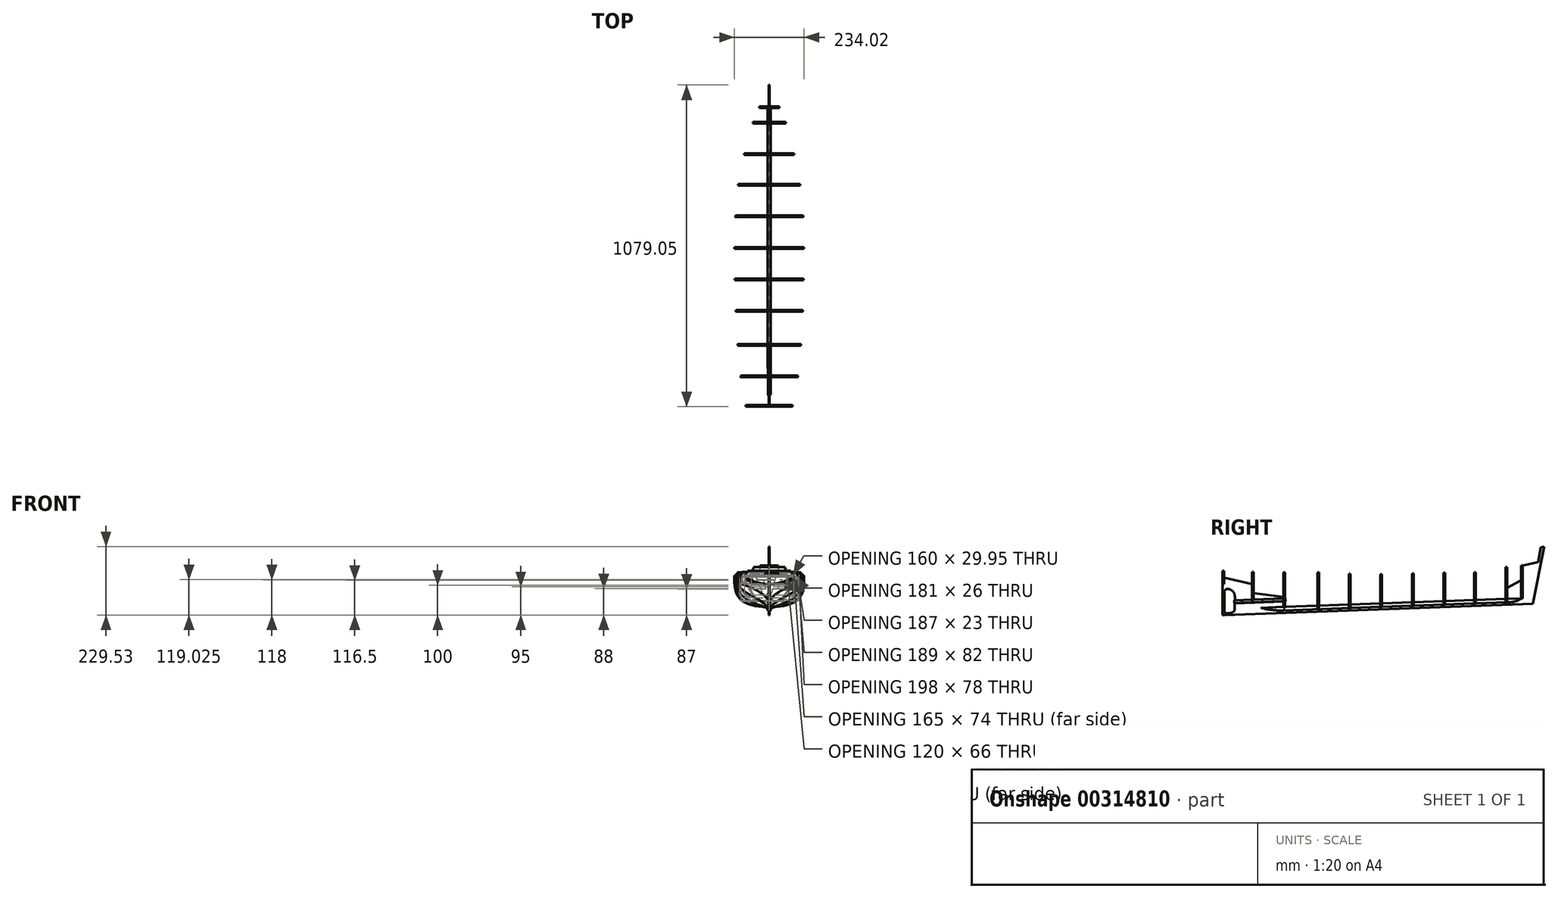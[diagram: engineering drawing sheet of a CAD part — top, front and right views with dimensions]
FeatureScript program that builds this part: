
annotation { "Feature Type Name" : "Feature", "Feature Type Description" : "" }
export const myFeature = defineFeature(function(context is Context, id is Id, definition is map)
    precondition{}
    {
        {
            var Q0;
            Q0=qCreatedBy(makeId("Front.planeOp"),FACE);
            cPlane(context, id + "F0", {"entities" : qUnion([Q0]), "cplaneType" : CPlaneType.OFFSET, "offset" : 99 * mm, "oppositeDirection" : true, "width" : 150 * mm, "height" : 150 * mm});
        }
        {
            var Q0;
            Q0=qCreatedBy(makeId("Front.planeOp"),FACE);
            cPlane(context, id + "F1", {"entities" : qUnion([Q0]), "cplaneType" : CPlaneType.OFFSET, "offset" : 204 * mm, "oppositeDirection" : true, "width" : 150 * mm, "height" : 150 * mm});
        }
        {
            var Q0;
            Q0=qCreatedBy(makeId("Front.planeOp"),FACE);
            cPlane(context, id + "F2", {"entities" : qUnion([Q0]), "cplaneType" : CPlaneType.OFFSET, "offset" : 319 * mm, "oppositeDirection" : true, "width" : 150 * mm, "height" : 150 * mm});
        }
        {
            var Q0;
            Q0=qCreatedBy(makeId("Front.planeOp"),FACE);
            cPlane(context, id + "F3", {"entities" : qUnion([Q0]), "cplaneType" : CPlaneType.OFFSET, "offset" : 424 * mm, "oppositeDirection" : true, "width" : 150 * mm, "height" : 150 * mm});
        }
        {
            var Q0;
            Q0=qCreatedBy(makeId("Front.planeOp"),FACE);
            cPlane(context, id + "F4", {"entities" : qUnion([Q0]), "cplaneType" : CPlaneType.OFFSET, "offset" : 530 * mm, "oppositeDirection" : true, "width" : 150 * mm, "height" : 150 * mm});
        }
        {
            var Q0;
            Q0=qCreatedBy(makeId("Front.planeOp"),FACE);
            cPlane(context, id + "F5", {"entities" : qUnion([Q0]), "cplaneType" : CPlaneType.OFFSET, "offset" : 636 * mm, "oppositeDirection" : true, "width" : 150 * mm, "height" : 150 * mm});
        }
        {
            var Q0;
            Q0=qCreatedBy(makeId("Front.planeOp"),FACE);
            cPlane(context, id + "F6", {"entities" : qUnion([Q0]), "cplaneType" : CPlaneType.OFFSET, "offset" : 742 * mm, "oppositeDirection" : true, "width" : 150 * mm, "height" : 150 * mm});
        }
        {
            var Q0;
            Q0=qCreatedBy(makeId("Front.planeOp"),FACE);
            cPlane(context, id + "F7", {"entities" : qUnion([Q0]), "cplaneType" : CPlaneType.OFFSET, "offset" : 844 * mm, "oppositeDirection" : true, "width" : 150 * mm, "height" : 150 * mm});
        }
        {
            var Q0;
            Q0=qCreatedBy(makeId("Front.planeOp"),FACE);
            cPlane(context, id + "F8", {"entities" : qUnion([Q0]), "cplaneType" : CPlaneType.OFFSET, "offset" : 950 * mm, "oppositeDirection" : true, "width" : 150 * mm, "height" : 150 * mm});
        }
        {
            var Q0;
            Q0=qCreatedBy(makeId("Front.planeOp"),FACE);
            cPlane(context, id + "F9", {"entities" : qUnion([Q0]), "cplaneType" : CPlaneType.OFFSET, "offset" : 1002 * mm, "oppositeDirection" : true, "width" : 150 * mm, "height" : 150 * mm});
        }
        {
            var Q0;
            Q0=qCreatedBy(makeId("Front.planeOp"),FACE);
            var sketch = newSketch(context, id + "F10", { "sketchPlane" : qUnion([Q0])});
            skLineSegment(sketch, "E0", {"start": v(-77.5, 50) * mm, "end": v(77.5, 50) * mm});
            skLineSegment(sketch, "E1", {"start": v(0, 64.94) * mm, "end": v(0, -64.32) * mm, "construction": true});
            skLineSegment(sketch, "E2", {"start": v(-77.5, 50) * mm, "end": v(-78.5, 29.02) * mm});
            skLineSegment(sketch, "E3", {"start": v(77.5, 50) * mm, "end": v(78.5, 29.02) * mm});
            skArc(sketch, "E4", {"start": v(-78.5, 29.02) * mm, "mid": v(-41.38, 12.02) * mm, "end": v(-1, 6) * mm});
            skArc(sketch, "E5", {"start": v(78.5, 29.02) * mm, "mid": v(41.38, 12.02) * mm, "end": v(1, 6) * mm});
            skLineSegment(sketch, "E6.bottom", {"start": v(-10, 43.5) * mm, "end": v(26, 43.5) * mm});
            skLineSegment(sketch, "E6.top", {"start": v(-10, 35.5) * mm, "end": v(26, 35.5) * mm});
            skArc(sketch, "E7", {"start": v(26, 35.5) * mm, "mid": v(30, 39.5) * mm, "end": v(26, 43.5) * mm});
            skArc(sketch, "E8", {"start": v(-10, 35.5) * mm, "mid": v(-14, 39.5) * mm, "end": v(-10, 43.5) * mm});
            skLineSegment(sketch, "E9", {"start": v(-1, 6) * mm, "end": v(-1, 29) * mm});
            skLineSegment(sketch, "E10", {"start": v(-1, 29) * mm, "end": v(1, 29) * mm});
            skLineSegment(sketch, "E11", {"start": v(1, 29) * mm, "end": v(1, 6) * mm});
            skPoint(sketch, "E12.orphan", {"position": v(0, 6) * mm});
            skLineSegment(sketch, "E13", {"start": v(75.13, 0) * mm, "end": v(-57.62, 0) * mm, "construction": true});
            skLineSegment(sketch, "E14", {"start": v(-77.73, 45.24) * mm, "end": v(-72.73, 45) * mm});
            skLineSegment(sketch, "E15", {"start": v(-72.73, 45) * mm, "end": v(-72.73, 50) * mm});
            skLineSegment(sketch, "E16", {"start": v(72.73, 50) * mm, "end": v(72.73, 45) * mm});
            skLineSegment(sketch, "E17", {"start": v(72.73, 45) * mm, "end": v(77.73, 45.16) * mm});
            skSolve(sketch);
        }
        {
            var Q0;
            Q0=qCreatedBy(id+"F0.planeOp",FACE);
            var sketch = newSketch(context, id + "F11", { "sketchPlane" : qUnion([Q0])});
            skLineSegment(sketch, "E18", {"start": v(0, 59) * mm, "end": v(0, -100.15) * mm, "construction": true});
            skLineSegment(sketch, "E19", {"start": v(-95, 46) * mm, "end": v(-96, 22.02) * mm});
            skLineSegment(sketch, "E20", {"start": v(95, 46) * mm, "end": v(96, 22.02) * mm});
            skArc(sketch, "E21", {"start": v(4, -48) * mm, "mid": v(2.67, -46.78) * mm, "end": v(1, -46.1) * mm});
            skPoint(sketch, "E22", {"position": v(-75, 0) * mm});
            skPoint(sketch, "E23", {"position": v(-27, -24.1) * mm});
            skPoint(sketch, "E24", {"position": v(27, -24.1) * mm});
            skPoint(sketch, "E25", {"position": v(75, 0) * mm});
            skPoint(sketch, "E26", {"position": v(-3, -51) * mm});
            skPoint(sketch, "E27", {"position": v(3, -51) * mm});
            skFitSpline(sketch, "E28", {"points": [v(-96, 22.02) * mm, v(-75, 0) * mm, v(-27, -24.1) * mm, v(-3, -51) * mm], "startDerivative": vector(-9.35, -169.5) * mm, "endDerivative": vector(26.1, -97.98) * mm});
            skFitSpline(sketch, "E29", {"points": [v(96, 22.02) * mm, v(75, 0) * mm, v(27, -24.1) * mm, v(3, -51) * mm], "startDerivative": vector(9.35, -169.5) * mm, "endDerivative": vector(-26.65, -99.36) * mm});
            skLineSegment(sketch, "E30", {"start": v(-1, -46.1) * mm, "end": v(-1, -24.1) * mm});
            skLineSegment(sketch, "E31", {"start": v(-1, -24.1) * mm, "end": v(1, -24.1) * mm});
            skLineSegment(sketch, "E32", {"start": v(1, -24.1) * mm, "end": v(1, -46.1) * mm});
            skArc(sketch, "E33.trimOffspring", {"start": v(-1, -46.1) * mm, "mid": v(-2.67, -46.78) * mm, "end": v(-4, -48) * mm});
            skLineSegment(sketch, "E34", {"start": v(-55, 6.05) * mm, "end": v(55, 6.05) * mm});
            skLineSegment(sketch, "E35", {"start": v(-55, 6.05) * mm, "end": v(-55, 11.05) * mm});
            skLineSegment(sketch, "E36", {"start": v(55, 6.05) * mm, "end": v(55, 11.05) * mm});
            skLineSegment(sketch, "E37", {"start": v(-80, 46) * mm, "end": v(-80, 31) * mm});
            skFitSpline(sketch, "E38", {"points": [v(-80, 31) * mm, v(-55, 11.05) * mm], "startDerivative": vector(0, -37.05) * mm, "endDerivative": vector(30.08, -12.67) * mm});
            skLineSegment(sketch, "E39", {"start": v(80, 31) * mm, "end": v(80, 46) * mm});
            skFitSpline(sketch, "E40", {"points": [v(80, 31) * mm, v(55, 11.05) * mm], "startDerivative": vector(0, -37.05) * mm, "endDerivative": vector(-36.33, -10.72) * mm});
            skLineSegment(sketch, "E41", {"start": v(-95, 46) * mm, "end": v(95, 46) * mm});
            skLineSegment(sketch, "E42", {"start": v(-80, 36) * mm, "end": v(80, 36) * mm});
            skLineSegment(sketch, "E43", {"start": v(-119.66, 0) * mm, "end": v(137.7, 0) * mm, "construction": true});
            skLineSegment(sketch, "E44", {"start": v(-90.2, 46) * mm, "end": v(-90.2, 41) * mm});
            skLineSegment(sketch, "E45", {"start": v(-90.2, 41) * mm, "end": v(-95.2, 41.2) * mm});
            skLineSegment(sketch, "E46", {"start": v(90.2, 46) * mm, "end": v(90.2, 41) * mm});
            skLineSegment(sketch, "E47", {"start": v(90.2, 41) * mm, "end": v(95.2, 41) * mm});
            skSolve(sketch);
        }
        {
            var Q0;
            Q0=qCreatedBy(id+"F1.planeOp",FACE);
            var sketch = newSketch(context, id + "F12", { "sketchPlane" : qUnion([Q0])});
            skLineSegment(sketch, "E48", {"start": v(0, 120.98) * mm, "end": v(0, -127) * mm, "construction": true});
            skLineSegment(sketch, "E49", {"start": v(-106, 45) * mm, "end": v(106, 45) * mm});
            skLineSegment(sketch, "E50", {"start": v(-5, -70) * mm, "end": v(5, -70) * mm});
            skLineSegment(sketch, "E51", {"start": v(-5, -70) * mm, "end": v(-5, -74) * mm});
            skLineSegment(sketch, "E52", {"start": v(5, -70) * mm, "end": v(5, -74) * mm});
            skCircle(sketch, "E53", {"center": v(0, -46.9) * mm, "radius": 5 * mm});
            skPoint(sketch, "E54", {"position": v(-100, -2) * mm});
            skPoint(sketch, "E55", {"position": v(-35, -46.9) * mm});
            skPoint(sketch, "E56", {"position": v(100, -2) * mm});
            skPoint(sketch, "E57", {"position": v(35, -46.9) * mm});
            skLineSegment(sketch, "E58", {"start": v(-83, 7) * mm, "end": v(83, 7) * mm});
            skLineSegment(sketch, "E59", {"start": v(-90.5, 33) * mm, "end": v(90.5, 33) * mm});
            skLineSegment(sketch, "E60", {"start": v(-90.5, 45) * mm, "end": v(-90.5, 25) * mm});
            skLineSegment(sketch, "E61", {"start": v(90.5, 45) * mm, "end": v(90.5, 25) * mm});
            skFitSpline(sketch, "E62", {"points": [v(-90.5, 25) * mm, v(-83, 7) * mm], "startDerivative": vector(0, -33.63) * mm, "endDerivative": vector(14.91, -11.46) * mm});
            skFitSpline(sketch, "E63", {"points": [v(90.5, 25) * mm, v(83, 7) * mm], "startDerivative": vector(0, -33.63) * mm, "endDerivative": vector(-14.91, -11.46) * mm});
            skLineSegment(sketch, "E64", {"start": v(-106, 45) * mm, "end": v(-106, 40) * mm});
            skLineSegment(sketch, "E65", {"start": v(106, 45) * mm, "end": v(106, 40) * mm});
            skFitSpline(sketch, "E66", {"points": [v(-5, -74) * mm, v(-35, -46.9) * mm, v(-100, -2) * mm, v(-106, 40) * mm], "startDerivative": vector(-39.15, 91.96) * mm, "endDerivative": vector(0, 150.68) * mm});
            skFitSpline(sketch, "E67", {"points": [v(5, -74) * mm, v(35, -46.9) * mm, v(100, -2) * mm, v(106, 40) * mm], "startDerivative": vector(39.15, 91.96) * mm, "endDerivative": vector(0, 150.68) * mm});
            skLineSegment(sketch, "E68", {"start": v(-137.52, 0) * mm, "end": v(170.84, 0) * mm, "construction": true});
            skLineSegment(sketch, "E69", {"start": v(-106, 40) * mm, "end": v(-101, 40) * mm});
            skLineSegment(sketch, "E70", {"start": v(-101, 40) * mm, "end": v(-101, 45) * mm});
            skLineSegment(sketch, "E71", {"start": v(106, 40) * mm, "end": v(101, 40) * mm});
            skLineSegment(sketch, "E72", {"start": v(101, 40) * mm, "end": v(101, 45) * mm});
            skSolve(sketch);
        }
        {
            var Q0;
            Q0=qCreatedBy(id+"F2.planeOp",FACE);
            var sketch = newSketch(context, id + "F13", { "sketchPlane" : qUnion([Q0])});
            skLineSegment(sketch, "E73", {"start": v(112, 45) * mm, "end": v(112, 36) * mm});
            skLineSegment(sketch, "E74", {"start": v(0, 101.57) * mm, "end": v(0, -139.56) * mm, "construction": true});
            skLineSegment(sketch, "E75", {"start": v(-5, -66.5) * mm, "end": v(5, -66.5) * mm});
            skLineSegment(sketch, "E76", {"start": v(5, -66.5) * mm, "end": v(5, -76.5) * mm});
            skLineSegment(sketch, "E77", {"start": v(-5, -66.5) * mm, "end": v(-5, -76.5) * mm});
            skCircle(sketch, "E78", {"center": v(0, -43) * mm, "radius": 5 * mm});
            skPoint(sketch, "E79", {"position": v(-110, 0) * mm});
            skPoint(sketch, "E80", {"position": v(-79, -43) * mm});
            skPoint(sketch, "E81", {"position": v(79, -43) * mm});
            skPoint(sketch, "E82", {"position": v(110, 0) * mm});
            skLineSegment(sketch, "E83", {"start": v(-90.5, 30) * mm, "end": v(90.5, 30) * mm});
            skLineSegment(sketch, "E84", {"start": v(93.5, 27) * mm, "end": v(93.5, 10) * mm});
            skLineSegment(sketch, "E85", {"start": v(90.5, 7) * mm, "end": v(-90.5, 7) * mm});
            skLineSegment(sketch, "E86", {"start": v(-93.5, 10) * mm, "end": v(-93.5, 27) * mm});
            skLineSegment(sketch, "E87", {"start": v(-112, 45) * mm, "end": v(112, 45) * mm});
            skLineSegment(sketch, "E88", {"start": v(-112, 45) * mm, "end": v(-112, 36) * mm});
            skLineSegment(sketch, "E89", {"start": v(-144, 0) * mm, "end": v(198.96, 0) * mm, "construction": true});
            skPoint(sketch, "E90", {"position": v(-26, -66.5) * mm});
            skPoint(sketch, "E91", {"position": v(26, -66.5) * mm});
            skFitSpline(sketch, "E92", {"points": [v(-112, 36) * mm, v(-110, 0) * mm, v(-79, -43) * mm, v(-26, -66.5) * mm, v(-5, -76.5) * mm], "startDerivative": vector(0, -205.14) * mm, "endDerivative": vector(105.65, -56.09) * mm});
            skFitSpline(sketch, "E93", {"points": [v(112, 36) * mm, v(110, 0) * mm, v(79, -43) * mm, v(26, -66.5) * mm, v(5, -76.5) * mm], "startDerivative": vector(0, -205.14) * mm, "endDerivative": vector(-105.65, -56.09) * mm});
            skLineSegment(sketch, "E94", {"start": v(-107, 36) * mm, "end": v(-107, 45) * mm});
            skLineSegment(sketch, "E95", {"start": v(107, 36) * mm, "end": v(107, 45) * mm});
            skPoint(sketch, "E96.visualSharp", {"position": v(-93.5, 30) * mm});
            skArc(sketch, "E96.filletArc", {"start": v(-90.5, 30) * mm, "mid": v(-92.62, 29.12) * mm, "end": v(-93.5, 27) * mm});
            skPoint(sketch, "E97.visualSharp", {"position": v(-93.5, 7) * mm});
            skArc(sketch, "E97.filletArc", {"start": v(-93.5, 10) * mm, "mid": v(-92.62, 7.88) * mm, "end": v(-90.5, 7) * mm});
            skPoint(sketch, "E98.visualSharp", {"position": v(93.5, 7) * mm});
            skArc(sketch, "E98.filletArc", {"start": v(90.5, 7) * mm, "mid": v(92.62, 7.88) * mm, "end": v(93.5, 10) * mm});
            skPoint(sketch, "E99.visualSharp", {"position": v(93.5, 30) * mm});
            skArc(sketch, "E99.filletArc", {"start": v(93.5, 27) * mm, "mid": v(92.62, 29.12) * mm, "end": v(90.5, 30) * mm});
            skLineSegment(sketch, "E100", {"start": v(107, 36) * mm, "end": v(112, 36) * mm});
            skLineSegment(sketch, "E101", {"start": v(-112, 36) * mm, "end": v(-107, 36) * mm});
            skSolve(sketch);
        }
        {
            var Q0;
            Q0=qCreatedBy(id+"F3.planeOp",FACE);
            var sketch = newSketch(context, id + "F14", { "sketchPlane" : qUnion([Q0])});
            skLineSegment(sketch, "E102", {"start": v(0, 107.4) * mm, "end": v(0, -128.62) * mm, "construction": true});
            skLineSegment(sketch, "E103", {"start": v(-5, -74) * mm, "end": v(-5, -62) * mm});
            skLineSegment(sketch, "E104", {"start": v(-5, -62) * mm, "end": v(5, -62) * mm});
            skLineSegment(sketch, "E105", {"start": v(5, -62) * mm, "end": v(5, -74) * mm});
            skPoint(sketch, "E106", {"position": v(-114, 0) * mm});
            skPoint(sketch, "E107", {"position": v(-63, -62) * mm});
            skPoint(sketch, "E108", {"position": v(63, -62) * mm});
            skPoint(sketch, "E109", {"position": v(114, 0) * mm});
            skLineSegment(sketch, "E110", {"start": v(-26.5, -52) * mm, "end": v(26.5, -52) * mm});
            skPoint(sketch, "E111", {"position": v(-85, -52) * mm});
            skPoint(sketch, "E112", {"position": v(85, -52) * mm});
            skLineSegment(sketch, "E113", {"start": v(94.5, 30) * mm, "end": v(-94.5, 30) * mm});
            skLineSegment(sketch, "E114", {"start": v(-115.5, 40) * mm, "end": v(115.5, 40) * mm});
            skLineSegment(sketch, "E115", {"start": v(-197.37, 0) * mm, "end": v(208.75, 0) * mm, "construction": true});
            skLineSegment(sketch, "E116", {"start": v(-115.5, 40) * mm, "end": v(-115.5, 20) * mm});
            skLineSegment(sketch, "E117", {"start": v(115.5, 40) * mm, "end": v(115.5, 20) * mm});
            skPoint(sketch, "E118", {"position": v(-108.5, -25) * mm});
            skFitSpline(sketch, "E119", {"points": [v(-115.5, 20) * mm, v(-114, 0) * mm, v(-108.5, -25) * mm, v(-85, -52) * mm, v(-63, -62) * mm, v(-5, -74) * mm], "startDerivative": vector(3.03, -113.75) * mm, "endDerivative": vector(234.8, -43.44) * mm});
            skPoint(sketch, "E120", {"position": v(108.5, -25) * mm});
            skFitSpline(sketch, "E121", {"points": [v(115.5, 20) * mm, v(114, 0) * mm, v(108.5, -25) * mm, v(85, -52) * mm, v(63, -62) * mm, v(5, -74) * mm], "startDerivative": vector(-9.17, -122.45) * mm, "endDerivative": vector(-239.88, -44.5) * mm});
            skFitSpline(sketch, "E122", {"points": [v(94.5, 30) * mm, v(26.5, -52) * mm], "startDerivative": vector(0.12, -163.2) * mm, "endDerivative": vector(-145.24, -36.05) * mm});
            skFitSpline(sketch, "E123", {"points": [v(-94.5, 30) * mm, v(-26.5, -52) * mm], "startDerivative": vector(-0.12, -163.2) * mm, "endDerivative": vector(145.24, -36.05) * mm});
            skLineSegment(sketch, "E124", {"start": v(-115.5, 35) * mm, "end": v(-110.5, 35) * mm});
            skLineSegment(sketch, "E125", {"start": v(-110.5, 35) * mm, "end": v(-110.5, 40) * mm});
            skLineSegment(sketch, "E126", {"start": v(110.5, 35) * mm, "end": v(110.5, 40) * mm});
            skLineSegment(sketch, "E127", {"start": v(110.5, 35) * mm, "end": v(115.5, 35) * mm});
            skSolve(sketch);
        }
        {
            var Q0;
            Q0=qCreatedBy(id+"F4.planeOp",FACE);
            var sketch = newSketch(context, id + "F15", { "sketchPlane" : qUnion([Q0])});
            skLineSegment(sketch, "E128", {"start": v(0, 104.32) * mm, "end": v(0, -131.94) * mm, "construction": true});
            skLineSegment(sketch, "E129", {"start": v(99, 29) * mm, "end": v(-99, 29) * mm});
            skLineSegment(sketch, "E130", {"start": v(-5, -59) * mm, "end": v(5, -59) * mm});
            skLineSegment(sketch, "E131", {"start": v(5, -59) * mm, "end": v(5, -71) * mm});
            skLineSegment(sketch, "E132", {"start": v(-5, -59) * mm, "end": v(-5, -71) * mm});
            skLineSegment(sketch, "E133", {"start": v(-50, -49) * mm, "end": v(50, -49) * mm});
            skLineSegment(sketch, "E134", {"start": v(50, -49) * mm, "end": v(50, -47.5) * mm});
            skLineSegment(sketch, "E135", {"start": v(-50, -49) * mm, "end": v(-50, -47.5) * mm});
            skPoint(sketch, "E136", {"position": v(-115.5, 0) * mm});
            skPoint(sketch, "E137", {"position": v(-92, -49) * mm});
            skPoint(sketch, "E138", {"position": v(115.5, 0) * mm});
            skPoint(sketch, "E139", {"position": v(92, -49) * mm});
            skFitSpline(sketch, "E140", {"points": [v(-99, 29) * mm, v(-50, -47.5) * mm], "startDerivative": vector(0.44, -158.46) * mm, "endDerivative": vector(93.73, -25.15) * mm});
            skFitSpline(sketch, "E141", {"points": [v(99, 29) * mm, v(50, -47.5) * mm], "startDerivative": vector(-0.44, -158.46) * mm, "endDerivative": vector(-93.73, -25.15) * mm});
            skLineSegment(sketch, "E142", {"start": v(-117, 39) * mm, "end": v(117, 39) * mm});
            skLineSegment(sketch, "E143", {"start": v(-174.19, 0) * mm, "end": v(198.17, 0) * mm, "construction": true});
            skPoint(sketch, "E144", {"position": v(-75.5, -59) * mm});
            skPoint(sketch, "E145", {"position": v(75.5, -59) * mm});
            skPoint(sketch, "E146", {"position": v(-108, -30) * mm});
            skPoint(sketch, "E147", {"position": v(108, -30) * mm});
            skLineSegment(sketch, "E148", {"start": v(-57, 39) * mm, "end": v(-57, 29) * mm});
            skLineSegment(sketch, "E149", {"start": v(57, 39) * mm, "end": v(57, 29) * mm});
            skLineSegment(sketch, "E150", {"start": v(-117, 34) * mm, "end": v(-112, 34) * mm});
            skLineSegment(sketch, "E151", {"start": v(-112, 34) * mm, "end": v(-112, 39) * mm});
            skLineSegment(sketch, "E152", {"start": v(117, 34) * mm, "end": v(112, 34) * mm});
            skLineSegment(sketch, "E153", {"start": v(112, 34) * mm, "end": v(112, 39) * mm});
            skFitSpline(sketch, "E154", {"points": [v(117, 34) * mm, v(115.5, 0) * mm, v(108, -30) * mm, v(92, -49) * mm, v(75.5, -59) * mm, v(5, -71) * mm], "startDerivative": vector(-2.98, -171.11) * mm, "endDerivative": vector(-315.56, 3.54) * mm});
            skLineSegment(sketch, "E155", {"start": v(117, 39) * mm, "end": v(117, 34) * mm});
            skLineSegment(sketch, "E156", {"start": v(-117, 39) * mm, "end": v(-117, 34) * mm});
            skFitSpline(sketch, "E157", {"points": [v(-117, 34) * mm, v(-115.5, 0) * mm, v(-108, -30) * mm, v(-92, -49) * mm, v(-75.5, -59) * mm, v(-5, -71) * mm], "startDerivative": vector(-2, -259.54) * mm, "endDerivative": vector(315.56, 3.54) * mm});
            skSolve(sketch);
        }
        {
            var Q0;
            Q0=qCreatedBy(id+"F5.planeOp",FACE);
            var sketch = newSketch(context, id + "F16", { "sketchPlane" : qUnion([Q0])});
            skLineSegment(sketch, "E158", {"start": v(-160.87, 0) * mm, "end": v(175.56, 0) * mm, "construction": true});
            skLineSegment(sketch, "E159", {"start": v(-113.5, 41) * mm, "end": v(113.5, 41) * mm});
            skLineSegment(sketch, "E160", {"start": v(0, 66.75) * mm, "end": v(0, -107.06) * mm, "construction": true});
            skLineSegment(sketch, "E161", {"start": v(-49.5, -45) * mm, "end": v(49.5, -45) * mm});
            skLineSegment(sketch, "E162", {"start": v(-5, -56) * mm, "end": v(5, -56) * mm});
            skLineSegment(sketch, "E163", {"start": v(-5, -56) * mm, "end": v(-5, -68) * mm});
            skLineSegment(sketch, "E164", {"start": v(5, -56) * mm, "end": v(5, -68) * mm});
            skLineSegment(sketch, "E165", {"start": v(-94.5, 31) * mm, "end": v(94.5, 31) * mm});
            skLineSegment(sketch, "E166", {"start": v(-49.5, -45) * mm, "end": v(-49.5, -43.5) * mm});
            skLineSegment(sketch, "E167", {"start": v(49.5, -45) * mm, "end": v(49.5, -43.5) * mm});
            skLineSegment(sketch, "E168", {"start": v(-113.5, 41) * mm, "end": v(-113.5, 36) * mm});
            skLineSegment(sketch, "E169", {"start": v(113.5, 41) * mm, "end": v(113.5, 36) * mm});
            skLineSegment(sketch, "E170", {"start": v(-113.5, 36) * mm, "end": v(-108.5, 36) * mm});
            skLineSegment(sketch, "E171", {"start": v(-108.5, 41) * mm, "end": v(-108.5, 36) * mm});
            skLineSegment(sketch, "E172", {"start": v(113.5, 36) * mm, "end": v(108.5, 36) * mm});
            skLineSegment(sketch, "E173", {"start": v(108.5, 36) * mm, "end": v(108.5, 41) * mm});
            skPoint(sketch, "E174", {"position": v(-111.5, 0) * mm});
            skPoint(sketch, "E175", {"position": v(-89, -45) * mm});
            skPoint(sketch, "E176", {"position": v(-73, -56) * mm});
            skPoint(sketch, "E177", {"position": v(-104, -25) * mm});
            skPoint(sketch, "E178", {"position": v(111.5, 0) * mm});
            skPoint(sketch, "E179", {"position": v(104, -25) * mm});
            skPoint(sketch, "E180", {"position": v(89, -45) * mm});
            skPoint(sketch, "E181", {"position": v(73, -56) * mm});
            skFitSpline(sketch, "E182", {"points": [v(-113.5, 36) * mm, v(-111.5, 0) * mm, v(-104, -25) * mm, v(-89, -45) * mm, v(-73, -56) * mm, v(-5, -68) * mm], "startDerivative": vector(-2.67, -184.28) * mm, "endDerivative": vector(453.64, -39.6) * mm});
            skFitSpline(sketch, "E183", {"points": [v(113.5, 36) * mm, v(111.5, 0) * mm, v(104, -25) * mm, v(89, -45) * mm, v(73, -56) * mm, v(5, -68) * mm], "startDerivative": vector(2.67, -184.28) * mm, "endDerivative": vector(-453.64, -39.6) * mm});
            skFitSpline(sketch, "E184.0", {"points": [v(94.47, 35.72) * mm, v(94.52, 32.1) * mm, v(94.5, 24.97) * mm, v(94.13, 16.53) * mm, v(93.6, 10.18) * mm, v(93.1, 5.66) * mm, v(92.48, 1.4) * mm, v(91.76, -2.5) * mm, v(90.92, -6.1) * mm, v(89.95, -9.4) * mm, v(89.02, -11.96) * mm, v(88.2, -13.94) * mm, v(87.53, -15.39) * mm, v(86.82, -16.81) * mm, v(86.03, -18.26) * mm, v(85.17, -19.7) * mm, v(83.94, -21.64) * mm, v(82.27, -24.02) * mm, v(80.1, -26.75) * mm, v(77.86, -29.27) * mm, v(75.62, -31.5) * mm, v(73.46, -33.4) * mm, v(71.3, -35.04) * mm, v(69.48, -36.26) * mm, v(67.94, -37.18) * mm, v(66.75, -37.84) * mm, v(65.51, -38.48) * mm, v(64.2, -39.11) * mm, v(62.9, -39.69) * mm, v(61.12, -40.42) * mm, v(58.66, -41.28) * mm, v(54.95, -42.33) * mm, v(50.19, -43.4) * mm, v(44.16, -44.49) * mm, v(36.67, -45.58) * mm, v(24.51, -47.07) * mm, v(12.69, -48.22) * mm, v(3.34, -49.04) * mm]});
            skFitSpline(sketch, "E185.0", {"points": [v(-94.47, 35.72) * mm, v(-94.52, 32.1) * mm, v(-94.5, 24.97) * mm, v(-94.13, 16.53) * mm, v(-93.6, 10.18) * mm, v(-93.1, 5.66) * mm, v(-92.48, 1.4) * mm, v(-91.76, -2.5) * mm, v(-90.92, -6.1) * mm, v(-89.95, -9.4) * mm, v(-89.02, -11.96) * mm, v(-88.2, -13.94) * mm, v(-87.53, -15.39) * mm, v(-86.82, -16.81) * mm, v(-86.03, -18.26) * mm, v(-85.17, -19.7) * mm, v(-83.94, -21.64) * mm, v(-82.27, -24.02) * mm, v(-80.1, -26.75) * mm, v(-77.86, -29.27) * mm, v(-75.62, -31.5) * mm, v(-73.46, -33.4) * mm, v(-71.3, -35.04) * mm, v(-69.48, -36.26) * mm, v(-67.94, -37.18) * mm, v(-66.75, -37.84) * mm, v(-65.51, -38.48) * mm, v(-64.2, -39.11) * mm, v(-62.9, -39.69) * mm, v(-61.12, -40.42) * mm, v(-58.66, -41.28) * mm, v(-54.95, -42.33) * mm, v(-50.19, -43.4) * mm, v(-44.16, -44.49) * mm, v(-36.67, -45.58) * mm, v(-24.51, -47.07) * mm, v(-12.69, -48.22) * mm, v(-3.34, -49.04) * mm]});
            skSolve(sketch);
        }
        {
            var Q0;
            Q0=qCreatedBy(id+"F6.planeOp",FACE);
            var sketch = newSketch(context, id + "F17", { "sketchPlane" : qUnion([Q0])});
            skLineSegment(sketch, "E186", {"start": v(-161.42, 0) * mm, "end": v(160.94, 0) * mm, "construction": true});
            skLineSegment(sketch, "E187", {"start": v(0, 71.63) * mm, "end": v(0, -107.97) * mm, "construction": true});
            skLineSegment(sketch, "E188", {"start": v(-104, 44) * mm, "end": v(104, 44) * mm});
            skLineSegment(sketch, "E189", {"start": v(-82.5, 34) * mm, "end": v(82.5, 34) * mm});
            skLineSegment(sketch, "E190", {"start": v(-50, -40) * mm, "end": v(50, -40) * mm});
            skLineSegment(sketch, "E191", {"start": v(-5, -51) * mm, "end": v(5, -51) * mm});
            skLineSegment(sketch, "E192", {"start": v(5, -51) * mm, "end": v(5, -63) * mm});
            skLineSegment(sketch, "E193", {"start": v(-5, -51) * mm, "end": v(-5, -63) * mm});
            skLineSegment(sketch, "E194", {"start": v(-50, -40) * mm, "end": v(-50, -32) * mm});
            skLineSegment(sketch, "E195", {"start": v(50, -40) * mm, "end": v(50, -32) * mm});
            skPoint(sketch, "E196", {"position": v(-95, 0) * mm});
            skPoint(sketch, "E197", {"position": v(95, 0) * mm});
            skPoint(sketch, "E198", {"position": v(-83, -25) * mm});
            skPoint(sketch, "E199", {"position": v(-71.5, -40) * mm});
            skPoint(sketch, "E200", {"position": v(71.5, -40) * mm});
            skPoint(sketch, "E201", {"position": v(83, -25) * mm});
            skPoint(sketch, "E202", {"position": v(-57, -51) * mm});
            skPoint(sketch, "E203", {"position": v(57, -51) * mm});
            skLineSegment(sketch, "E204", {"start": v(-104, 44) * mm, "end": v(-104, 39) * mm});
            skLineSegment(sketch, "E205", {"start": v(-104, 39) * mm, "end": v(-99, 39) * mm});
            skLineSegment(sketch, "E206", {"start": v(-99, 39) * mm, "end": v(-99, 44) * mm});
            skLineSegment(sketch, "E207", {"start": v(104, 44) * mm, "end": v(104, 39) * mm});
            skLineSegment(sketch, "E208", {"start": v(104, 39) * mm, "end": v(99, 39) * mm});
            skLineSegment(sketch, "E209", {"start": v(99, 39) * mm, "end": v(99, 44) * mm});
            skFitSpline(sketch, "E210", {"points": [v(-104, 39) * mm, v(-95, 0) * mm, v(-83, -25) * mm, v(-71.5, -40) * mm, v(-57, -51) * mm, v(-5, -63) * mm], "startDerivative": vector(34.6, -155.2) * mm, "endDerivative": vector(282.41, -23.43) * mm});
            skFitSpline(sketch, "E211", {"points": [v(104, 39) * mm, v(95, 0) * mm, v(83, -25) * mm, v(71.5, -40) * mm, v(57, -51) * mm, v(5, -63) * mm], "startDerivative": vector(-34.6, -155.2) * mm, "endDerivative": vector(-282.41, -23.43) * mm});
            skFitSpline(sketch, "E212", {"points": [v(-82.5, 34) * mm, v(-50, -32) * mm], "startDerivative": vector(9.01, -85.28) * mm, "endDerivative": vector(62.27, -47.38) * mm});
            skFitSpline(sketch, "E213", {"points": [v(50, -32) * mm, v(82.5, 34) * mm], "startDerivative": vector(62.27, 47.38) * mm, "endDerivative": vector(9.01, 85.28) * mm});
            skSolve(sketch);
        }
        {
            var Q0;
            Q0=qCreatedBy(id+"F7.planeOp",FACE);
            var sketch = newSketch(context, id + "F18", { "sketchPlane" : qUnion([Q0])});
            skLineSegment(sketch, "E214", {"start": v(-169.71, 0) * mm, "end": v(174.28, 0) * mm, "construction": true});
            skLineSegment(sketch, "E215", {"start": v(0, 106.1) * mm, "end": v(0, -104.68) * mm, "construction": true});
            skLineSegment(sketch, "E216", {"start": v(-85, 45) * mm, "end": v(85, 45) * mm});
            skLineSegment(sketch, "E217", {"start": v(-60, 35) * mm, "end": v(60, 35) * mm});
            skLineSegment(sketch, "E218", {"start": v(-26, -31) * mm, "end": v(26, -31) * mm});
            skLineSegment(sketch, "E219", {"start": v(-5, -60.5) * mm, "end": v(-5, -48.5) * mm});
            skLineSegment(sketch, "E220", {"start": v(-5, -48.5) * mm, "end": v(5, -48.5) * mm});
            skLineSegment(sketch, "E221", {"start": v(5, -48.5) * mm, "end": v(5, -60.5) * mm});
            skPoint(sketch, "E222", {"position": v(-69, 0) * mm});
            skPoint(sketch, "E223", {"position": v(-51, -31) * mm});
            skPoint(sketch, "E224", {"position": v(-33, -48.5) * mm});
            skPoint(sketch, "E224.positionSnap0", {"position": v(0, -48.5) * mm});
            skPoint(sketch, "E225", {"position": v(33, -48.5) * mm});
            skPoint(sketch, "E226", {"position": v(51, -31) * mm});
            skPoint(sketch, "E227", {"position": v(69, 0) * mm});
            skLineSegment(sketch, "E228", {"start": v(-80, 45) * mm, "end": v(-80, 40) * mm});
            skLineSegment(sketch, "E229", {"start": v(-85, 45) * mm, "end": v(-84, 40) * mm});
            skLineSegment(sketch, "E230", {"start": v(-84, 40) * mm, "end": v(-80, 40) * mm});
            skLineSegment(sketch, "E231", {"start": v(80, 45) * mm, "end": v(80, 40) * mm});
            skLineSegment(sketch, "E232", {"start": v(80, 40) * mm, "end": v(84, 40) * mm});
            skLineSegment(sketch, "E233", {"start": v(84, 40) * mm, "end": v(85, 45) * mm});
            skFitSpline(sketch, "E234", {"points": [v(-84, 40) * mm, v(-69, 0) * mm, v(-51, -31) * mm, v(-33, -48.5) * mm, v(-5, -60.5) * mm], "startDerivative": vector(43.97, -145.23) * mm, "endDerivative": vector(125.12, -29.34) * mm});
            skFitSpline(sketch, "E235", {"points": [v(5, -60.5) * mm, v(33, -48.5) * mm, v(51, -31) * mm, v(69, 0) * mm, v(84, 40) * mm], "startDerivative": vector(125.12, 29.34) * mm, "endDerivative": vector(43.97, 145.23) * mm});
            skFitSpline(sketch, "E236", {"points": [v(60, 35) * mm, v(26, -31) * mm], "startDerivative": vector(-16.77, -77.95) * mm, "endDerivative": vector(-59.34, -57.1) * mm});
            skFitSpline(sketch, "E237", {"points": [v(-60, 35) * mm, v(-26, -31) * mm], "startDerivative": vector(16.77, -77.95) * mm, "endDerivative": vector(59.34, -57.1) * mm});
            skLineSegment(sketch, "E238", {"start": v(-33, 45) * mm, "end": v(-33, 35) * mm});
            skLineSegment(sketch, "E239", {"start": v(33, 45) * mm, "end": v(33, 35) * mm});
            skSolve(sketch);
        }
        {
            var Q0;
            Q0=qCreatedBy(id+"F8.planeOp",FACE);
            var sketch = newSketch(context, id + "F19", { "sketchPlane" : qUnion([Q0])});
            skLineSegment(sketch, "E240", {"start": v(-111.78, 0) * mm, "end": v(108.37, 0) * mm, "construction": true});
            skLineSegment(sketch, "E241", {"start": v(0, 65.56) * mm, "end": v(0, -64.3) * mm, "construction": true});
            skLineSegment(sketch, "E242", {"start": v(-57.5, 63) * mm, "end": v(57.5, 63) * mm});
            skLineSegment(sketch, "E243", {"start": v(-5, -44) * mm, "end": v(5, -44) * mm});
            skLineSegment(sketch, "E244", {"start": v(5, -44) * mm, "end": v(5, -51) * mm});
            skLineSegment(sketch, "E245", {"start": v(-5, -44) * mm, "end": v(-5, -51) * mm});
            skPoint(sketch, "E246", {"position": v(-33, 0) * mm});
            skPoint(sketch, "E247", {"position": v(33, 0) * mm});
            skFitSpline(sketch, "E248", {"points": [v(-57.5, 63) * mm, v(-33, 0) * mm, v(-5, -51) * mm], "startDerivative": vector(51.14, -123.86) * mm, "endDerivative": vector(82.4, -94.53) * mm});
            skFitSpline(sketch, "E249", {"points": [v(5, -51) * mm, v(33, 0) * mm, v(57.5, 63) * mm], "startDerivative": vector(82.4, 94.53) * mm, "endDerivative": vector(51.14, 123.86) * mm});
            skLineSegment(sketch, "E250", {"start": v(-52.5, 63) * mm, "end": v(-52.5, 58) * mm});
            skLineSegment(sketch, "E251", {"start": v(-52.5, 58) * mm, "end": v(-55.46, 58) * mm});
            skLineSegment(sketch, "E252", {"start": v(52.5, 63) * mm, "end": v(52.5, 58) * mm});
            skPoint(sketch, "E252.endSnap0", {"position": v(-53.98, 58) * mm});
            skLineSegment(sketch, "E253", {"start": v(52.5, 58) * mm, "end": v(55.46, 58) * mm});
            skSolve(sketch);
        }
        {
            var Q0;
            Q0=qCreatedBy(id+"F9.planeOp",FACE);
            var sketch = newSketch(context, id + "F20", { "sketchPlane" : qUnion([Q0])});
            skLineSegment(sketch, "E254", {"start": v(-71.76, 0) * mm, "end": v(82.77, 0) * mm, "construction": true});
            skLineSegment(sketch, "E255", {"start": v(0, 59.99) * mm, "end": v(0, -53.53) * mm, "construction": true});
            skLineSegment(sketch, "E256", {"start": v(-35.5, 68) * mm, "end": v(-30.5, 68) * mm});
            skLineSegment(sketch, "E257", {"start": v(-2, -42) * mm, "end": v(-1, -42) * mm});
            skLineSegment(sketch, "E258", {"start": v(-1, -42) * mm, "end": v(-1, 20) * mm});
            skLineSegment(sketch, "E259", {"start": v(-1, 20) * mm, "end": v(1, 20) * mm});
            skLineSegment(sketch, "E260", {"start": v(1, 20) * mm, "end": v(1, -42) * mm});
            skLineSegment(sketch, "E261", {"start": v(1, -42) * mm, "end": v(2, -42) * mm});
            skPoint(sketch, "E262", {"position": v(-15, 0) * mm});
            skPoint(sketch, "E263", {"position": v(15, 0) * mm});
            skFitSpline(sketch, "E264", {"points": [v(-35.5, 68) * mm, v(-15, 0) * mm, v(-2, -42) * mm], "startDerivative": vector(55.47, -158.5) * mm, "endDerivative": vector(34.43, -88.98) * mm});
            skFitSpline(sketch, "E265", {"points": [v(2, -42) * mm, v(15, 0) * mm, v(35.5, 68) * mm], "startDerivative": vector(34.43, 88.98) * mm, "endDerivative": vector(55.47, 158.5) * mm});
            skLineSegment(sketch, "E266", {"start": v(-30.5, 68) * mm, "end": v(-30.5, 63) * mm});
            skLineSegment(sketch, "E267", {"start": v(-30.5, 63) * mm, "end": v(-33.77, 63) * mm});
            skLineSegment(sketch, "E268", {"start": v(30.5, 68) * mm, "end": v(30.5, 63) * mm});
            skLineSegment(sketch, "E269", {"start": v(30.5, 63) * mm, "end": v(33.77, 63) * mm});
            skLineSegment(sketch, "E270", {"start": v(-30.5, 68) * mm, "end": v(30.5, 68) * mm});
            skLineSegment(sketch, "E271", {"start": v(30.5, 68) * mm, "end": v(35.5, 68) * mm});
            skLineSegment(sketch, "E272", {"start": v(33.77, 63) * mm, "end": v(33.77, 63) * mm});
            skSolve(sketch);
        }
        {
            var Q0;
            {var subQ6=sQuery(id+"F10.wireOp",EDGE,"E4");Q0=makeQuery(id+"F10.imprint","IMPRINT",FACE,{"disambiguationData":[TD([[makeQuery(id+"F10.imprint","IMPRINT",EDGE,{"derivedFrom":subQ6}),1.0]])]});}
            extrude(context, id + "F21", {"entities" : qUnion([Q0]), "oppositeDirection" : true, "depth" : 5 * mm});
        }
        {
            var Q0;
            Q0=makeQuery(id+"F11.imprint","IMPRINT",FACE,{"disambiguationData":[TD([[makeQuery(id+"F11.imprint","IMPRINT",EDGE,{"derivedFrom":sQuery(id+"F11.wireOp",EDGE,"E21")}),-1.0]])]});
            var Q1;
            {var subQ3=sQuery(id+"F11.wireOp",EDGE,"E42");Q1=makeQuery(id+"F11.imprint","IMPRINT",FACE,{"disambiguationData":[TD([[makeQuery(id+"F11.imprint","IMPRINT",EDGE,{"derivedFrom":subQ3}),1.0]])]});}
            extrude(context, id + "F22", {"entities" : qUnion([Q0, Q1]), "oppositeDirection" : true, "depth" : 5 * mm});
        }
        {
            var Q0;
            Q0=makeQuery(id+"F12.imprint","IMPRINT",FACE,{"disambiguationData":[TD([[makeQuery(id+"F12.imprint","IMPRINT",EDGE,{"derivedFrom":sQuery(id+"F12.wireOp",EDGE,"E50")}),1.0]])]});
            var Q1;
            {var subQ5=sQuery(id+"F12.wireOp",EDGE,"E59");Q1=makeQuery(id+"F12.imprint","IMPRINT",FACE,{"disambiguationData":[TD([[makeQuery(id+"F12.imprint","IMPRINT",EDGE,{"derivedFrom":subQ5}),1.0]])]});}
            extrude(context, id + "F23", {"entities" : qUnion([Q0, Q1]), "oppositeDirection" : true, "depth" : 5 * mm});
        }
        {
            var Q0;
            Q0=makeQuery(id+"F13.imprint","IMPRINT",FACE,{"disambiguationData":[TD([[makeQuery(id+"F13.imprint","IMPRINT",EDGE,{"derivedFrom":sQuery(id+"F13.wireOp",EDGE,"E75")}),1.0]])]});
            extrude(context, id + "F24", {"entities" : qUnion([Q0]), "oppositeDirection" : true, "depth" : 5 * mm});
        }
        {
            var Q0;
            Q0=makeQuery(id+"F14.imprint","IMPRINT",FACE,{"disambiguationData":[TD([[makeQuery(id+"F14.imprint","IMPRINT",EDGE,{"derivedFrom":sQuery(id+"F14.wireOp",EDGE,"E103")}),1.0]])]});
            extrude(context, id + "F25", {"entities" : qUnion([Q0]), "oppositeDirection" : true, "depth" : 5 * mm});
        }
        {
            var Q0;
            Q0=makeQuery(id+"F15.imprint","IMPRINT",FACE,{"disambiguationData":[TD([[makeQuery(id+"F15.imprint","IMPRINT",EDGE,{"derivedFrom":sQuery(id+"F15.wireOp",EDGE,"E130")}),1.0]])]});
            var Q1;
            {var subQ0=sQuery(id+"F15.wireOp",EDGE,"E148");Q1=makeQuery(id+"F15.imprint","IMPRINT",FACE,{"disambiguationData":[TD([[makeQuery(id+"F15.imprint","IMPRINT",EDGE,{"derivedFrom":subQ0}),1.0]])]});}
            extrude(context, id + "F26", {"entities" : qUnion([Q0, Q1]), "oppositeDirection" : true, "depth" : 5 * mm});
        }
        {
            var Q0;
            Q0=makeQuery(id+"F16.imprint","IMPRINT",FACE,{"disambiguationData":[TD([[makeQuery(id+"F16.imprint","IMPRINT",EDGE,{"derivedFrom":sQuery(id+"F16.wireOp",EDGE,"E161")}),-1.0]])]});
            extrude(context, id + "F27", {"entities" : qUnion([Q0]), "oppositeDirection" : true, "depth" : 5 * mm});
        }
        {
            var Q0;
            Q0=makeQuery(id+"F17.imprint","IMPRINT",FACE,{"disambiguationData":[TD([[makeQuery(id+"F17.imprint","IMPRINT",EDGE,{"derivedFrom":sQuery(id+"F17.wireOp",EDGE,"E189")}),1.0]])]});
            extrude(context, id + "F28", {"entities" : qUnion([Q0]), "oppositeDirection" : true, "depth" : 5 * mm});
        }
        {
            var Q0;
            Q0=makeQuery(id+"F18.imprint","IMPRINT",FACE,{"disambiguationData":[TD([[makeQuery(id+"F18.imprint","IMPRINT",EDGE,{"derivedFrom":sQuery(id+"F18.wireOp",EDGE,"E218")}),-1.0]])]});
            var Q1;
            {var subQ0=sQuery(id+"F18.wireOp",EDGE,"E238");Q1=makeQuery(id+"F18.imprint","IMPRINT",FACE,{"disambiguationData":[TD([[makeQuery(id+"F18.imprint","IMPRINT",EDGE,{"derivedFrom":subQ0}),1.0]])]});}
            extrude(context, id + "F29", {"entities" : qUnion([Q0, Q1]), "oppositeDirection" : true, "depth" : 5 * mm});
        }
        {
            var Q0;
            Q0=makeQuery(id+"F19.imprint","IMPRINT",FACE,{"disambiguationData":[TD([[makeQuery(id+"F19.imprint","IMPRINT",EDGE,{"derivedFrom":sQuery(id+"F19.wireOp",EDGE,"E243")}),1.0]])]});
            extrude(context, id + "F30", {"entities" : qUnion([Q0]), "oppositeDirection" : true, "depth" : 5 * mm});
        }
        {
            var Q0;
            Q0=makeQuery(id+"F20.imprint","IMPRINT",FACE,{"disambiguationData":[TD([[makeQuery(id+"F20.imprint","IMPRINT",EDGE,{"derivedFrom":sQuery(id+"F20.wireOp",EDGE,"E257")}),1.0]])]});
            extrude(context, id + "F31", {"entities" : qUnion([Q0]), "oppositeDirection" : true, "depth" : 5 * mm});
        }
        {
            var Q0;
            Q0=qCreatedBy(makeId("Right.planeOp"),FACE);
            var sketch = newSketch(context, id + "F32", { "sketchPlane" : qUnion([Q0])});
            skLineSegment(sketch, "E273", {"start": v(319, -43) * mm, "end": v(99, -51) * mm, "construction": true});
            skLineSegment(sketch, "E274", {"start": v(203.9, -52.78) * mm, "end": v(41, -58.7) * mm});
            skLineSegment(sketch, "E275", {"start": v(204, -42.77) * mm, "end": v(41.1, -48.7) * mm});
            skLineSegment(sketch, "E276", {"start": v(6, -98) * mm, "end": v(955, -63.5) * mm});
            skLineSegment(sketch, "E277", {"start": v(128, -73.55) * mm, "end": v(955, -43.48) * mm});
            skLineSegment(sketch, "E278", {"start": v(204, -42.77) * mm, "end": v(204, -36.77) * mm});
            skLineSegment(sketch, "E279", {"start": v(0, 124.87) * mm, "end": v(0, -146.2) * mm, "construction": true});
            skLineSegment(sketch, "E280", {"start": v(0, -98) * mm, "end": v(6, -98) * mm});
            skLineSegment(sketch, "E281", {"start": v(99, -51) * mm, "end": v(0, -54.6) * mm, "construction": true});
            skLineSegment(sketch, "E282", {"start": v(0, -98) * mm, "end": v(0, 28) * mm});
            skLineSegment(sketch, "E283", {"start": v(0, 28) * mm, "end": v(99, 6.45) * mm});
            skLineSegment(sketch, "E284", {"start": v(99, 6.45) * mm, "end": v(99, -24.57) * mm});
            skLineSegment(sketch, "E285", {"start": v(99, -24.57) * mm, "end": v(204, -36.77) * mm});
            skLineSegment(sketch, "E286", {"start": v(6, -20.58) * mm, "end": v(6, -86.81) * mm});
            skLineSegment(sketch, "E287", {"start": v(11.18, -91.8) * mm, "end": v(26.55, -91.25) * mm});
            skLineSegment(sketch, "E288", {"start": v(41.1, -48.7) * mm, "end": v(41.1, -35.58) * mm});
            skLineSegment(sketch, "E289", {"start": v(41, -58.7) * mm, "end": v(41, -76.26) * mm});
            skLineSegment(sketch, "E290", {"start": v(-122.84, -98) * mm, "end": v(1088.19, -98) * mm, "construction": true});
            skLineSegment(sketch, "E291", {"start": v(204, -82.8) * mm, "end": v(955, -55.49) * mm});
            skLineSegment(sketch, "E292", {"start": v(204, -82.8) * mm, "end": v(204, -90.8) * mm});
            skPoint(sketch, "E293.visualSharp", {"position": v(6, -92) * mm});
            skArc(sketch, "E293.filletArc", {"start": v(6, -86.81) * mm, "mid": v(7.53, -90.41) * mm, "end": v(11.18, -91.8) * mm});
            skPoint(sketch, "E294.visualSharp", {"position": v(41, -90.72) * mm});
            skArc(sketch, "E294.filletArc", {"start": v(26.55, -91.25) * mm, "mid": v(36.8, -86.67) * mm, "end": v(41, -76.26) * mm});
            skPoint(sketch, "E295.visualSharp", {"position": v(41.1, -9.67) * mm});
            skPoint(sketch, "E296.visualSharp", {"position": v(6, -10.94) * mm});
            skLineSegment(sketch, "E297", {"start": v(204, -82.8) * mm, "end": v(204, -70.79) * mm});
            skFitSpline(sketch, "E298", {"points": [v(128, -73.55) * mm, v(204, -82.8) * mm], "startDerivative": vector(72.42, -19.7) * mm, "endDerivative": vector(79.04, 2.13) * mm});
            skLineSegment(sketch, "E299", {"start": v(203.9, -52.78) * mm, "end": v(204, -70.79) * mm});
            skLineSegment(sketch, "E300", {"start": v(204, 7.6) * mm, "end": v(204, -131.97) * mm, "construction": true});
            skArc(sketch, "E301", {"start": v(15.93, -10.58) * mm, "mid": v(8.9, -13.54) * mm, "end": v(6, -20.58) * mm});
            skArc(sketch, "E302", {"start": v(41.1, -35.58) * mm, "mid": v(33.72, -17.84) * mm, "end": v(15.93, -10.58) * mm});
            skLineSegment(sketch, "E303", {"start": v(1040.94, -60.37) * mm, "end": v(1079.05, 131.53) * mm});
            skLineSegment(sketch, "E304", {"start": v(1079.05, 131.53) * mm, "end": v(1068.36, 129.04) * mm});
            skLineSegment(sketch, "E305", {"start": v(1068.36, 129.04) * mm, "end": v(1058.62, 80) * mm});
            skLineSegment(sketch, "E306", {"start": v(1058.62, 80) * mm, "end": v(1007, 68) * mm});
            skLineSegment(sketch, "E307", {"start": v(1007, 68) * mm, "end": v(1007, 19) * mm});
            skLineSegment(sketch, "E308", {"start": v(1007, 19) * mm, "end": v(1002, 19) * mm});
            skLineSegment(sketch, "E309", {"start": v(1002, 19) * mm, "end": v(955, -6.48) * mm});
            skLineSegment(sketch, "E310", {"start": v(955, -6.48) * mm, "end": v(955, -63.5) * mm});
            skLineSegment(sketch, "E311", {"start": v(955, -63.5) * mm, "end": v(1040.94, -60.37) * mm});
            skLineSegment(sketch, "E312", {"start": v(955, -43.48) * mm, "end": v(1001.97, -41.77) * mm});
            skFitSpline(sketch, "E313", {"points": [v(955, -55.49) * mm, v(1001.97, -41.77) * mm], "startDerivative": vector(50.69, 2.41) * mm, "endDerivative": vector(37.75, 34.47) * mm});
            skSolve(sketch);
        }
        {
            var Q0;
            Q0=makeQuery(id+"F32.imprint","IMPRINT",FACE,{"disambiguationData":[TD([[makeQuery(id+"F32.imprint","IMPRINT",EDGE,{"derivedFrom":sQuery(id+"F32.wireOp",EDGE,"E274")}),1.0]])]});
            var Q1;
            {var subQ2=sQuery(id+"F32.wireOp",EDGE,"E297");Q1=makeQuery(id+"F32.imprint","IMPRINT",FACE,{"disambiguationData":[TD([[makeQuery(id+"F32.imprint","IMPRINT",EDGE,{"derivedFrom":subQ2}),1.0]])]});}
            var Q2;
            {var subQ4=sQuery(id+"F32.wireOp",EDGE,"E291");Q2=makeQuery(id+"F32.imprint","IMPRINT",FACE,{"disambiguationData":[TD([[makeQuery(id+"F32.imprint","IMPRINT",EDGE,{"derivedFrom":subQ4}),1.0]])]});}
            var Q3;
            {var subQ4=sQuery(id+"F32.wireOp",EDGE,"E291");Q3=makeQuery(id+"F32.imprint","IMPRINT",FACE,{"disambiguationData":[TD([[makeQuery(id+"F32.imprint","IMPRINT",EDGE,{"derivedFrom":subQ4}),-1.0]])]});}
            var Q4;
            {var subQ0=sQuery(id+"F32.wireOp",EDGE,"ff7c8b0a-bd72-45e8-9ee2-0653f121e551");Q4=makeQuery(id+"F32.imprint","IMPRINT",FACE,{"disambiguationData":[TD([[makeQuery(id+"F32.imprint","IMPRINT",EDGE,{"derivedFrom":subQ0}),1.0]])]});}
            var Q5;
            Q5=makeQuery(id+"F32.imprint","IMPRINT",FACE,{"disambiguationData":[TD([[makeQuery(id+"F32.imprint","IMPRINT",EDGE,{"derivedFrom":sQuery(id+"F32.wireOp",EDGE,"E303")}),1.0]])]});
            var Q6;
            {var subQ0=sQuery(id+"F32.wireOp",EDGE,"E312");Q6=makeQuery(id+"F32.imprint","IMPRINT",FACE,{"disambiguationData":[TD([[makeQuery(id+"F32.imprint","IMPRINT",EDGE,{"derivedFrom":subQ0}),-1.0]])]});}
            extrude(context, id + "F33", {"entities" : qUnion([Q0, Q1, Q2, Q3, Q4, Q5, Q6]), "endBound" : BoundingType.SYMMETRIC, "depth" : 2 * mm});
        }
        {
            var Q0;
            {var subQ2=sQuery(id+"F32.wireOp",EDGE,"E297");Q0=makeQuery(id+"F32.imprint","IMPRINT",FACE,{"disambiguationData":[TD([[makeQuery(id+"F32.imprint","IMPRINT",EDGE,{"derivedFrom":subQ2}),1.0]])]});}
            var Q1;
            {var subQ4=sQuery(id+"F32.wireOp",EDGE,"E291");Q1=makeQuery(id+"F32.imprint","IMPRINT",FACE,{"disambiguationData":[TD([[makeQuery(id+"F32.imprint","IMPRINT",EDGE,{"derivedFrom":subQ4}),1.0]])]});}
            var Q2;
            {var subQ0=sQuery(id+"F32.wireOp",EDGE,"E312");Q2=makeQuery(id+"F32.imprint","IMPRINT",FACE,{"disambiguationData":[TD([[makeQuery(id+"F32.imprint","IMPRINT",EDGE,{"derivedFrom":subQ0}),-1.0]])]});}
            extrude(context, id + "F34", {"entities" : qUnion([Q0, Q1, Q2]), "operationType" : NewBodyOperationType.ADD, "endBound" : BoundingType.SYMMETRIC, "depth" : 10 * mm});
        }
        {
            var Q0;
            Q0=sQuery(id+"F32.wireOp",EDGE,"E281");
            var Q1;
            Q1=sQuery(id+"F32.wireOp",VERTEX,"E275.end");
            cPlane(context, id + "F35", {"entities" : qUnion([Q0, Q1]), "cplaneType" : CPlaneType.LINE_POINT, "offset" : 25 * mm, "width" : 150 * mm, "height" : 150 * mm});
        }
        {
            var Q0;
            Q0=qCreatedBy(id+"F35.planeOp",FACE);
            var sketch = newSketch(context, id + "F36", { "sketchPlane" : qUnion([Q0])});
            skCircle(sketch, "E314", {"center": v(0, -54.64) * mm, "radius": 4.49 * mm});
            skSolve(sketch);
        }
        {
            var Q0;
            Q0=makeQuery(id+"F36.imprint","IMPRINT",FACE,{"disambiguationData":[TD([[makeQuery(id+"F36.imprint","IMPRINT",EDGE,{"derivedFrom":sQuery(id+"F36.wireOp",EDGE,"E314")}),1.0]])]});
            extrude(context, id + "F37", {"entities" : qUnion([Q0]), "depth" : 2 * mm, "hasSecondDirection" : true, "secondDirectionOppositeDirection" : true, "secondDirectionDepth" : 170 * mm});
        }
    });
